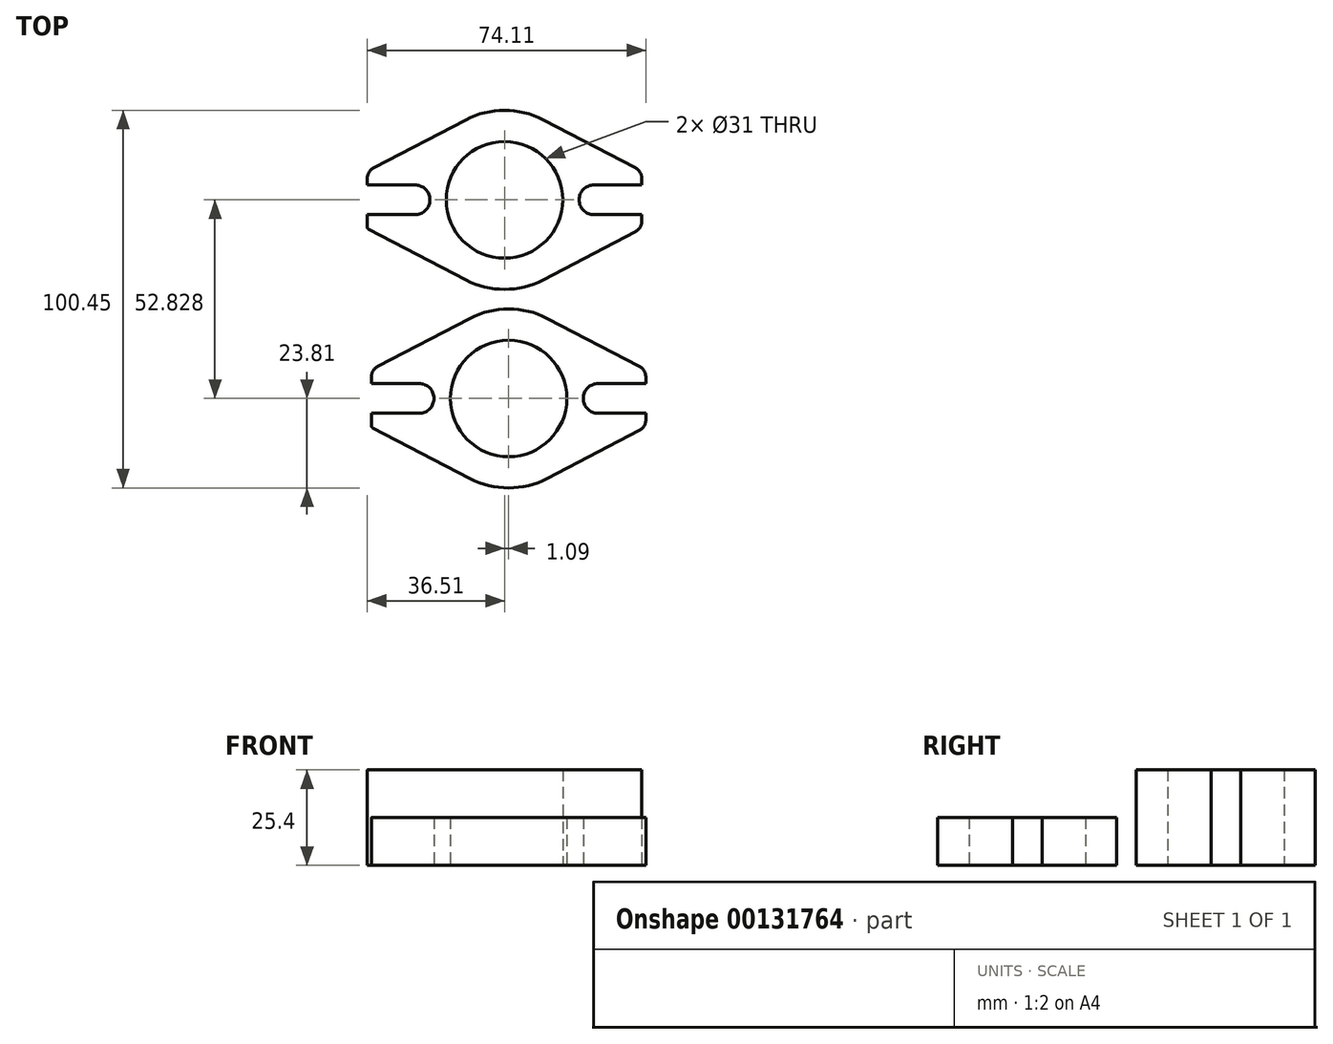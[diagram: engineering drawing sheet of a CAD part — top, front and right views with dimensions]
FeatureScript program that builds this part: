
annotation { "Feature Type Name" : "Feature", "Feature Type Description" : "" }
export const myFeature = defineFeature(function(context is Context, id is Id, definition is map)
    precondition{}
    {
        {
            var Q0;
            Q0=qCreatedBy(makeId("Top.planeOp"), FACE);
            var sketch = newSketch(context, id + "F0", { "sketchPlane" : qUnion([Q0])});
            skLineSegment(sketch, "E0.left", {"start": v(36.51, -5.7) * mm, "end": v(36.51, -3.96) * mm});
            skLineSegment(sketch, "E0.right", {"start": v(-36.51, -7.23) * mm, "end": v(-36.51, -3.96) * mm});
            skPoint(sketch, "E0.middle", {"position": v(0, 0) * mm});
            skArc(sketch, "E1", {"start": v(-23.81, -3.96) * mm, "mid": v(-19.85, 0) * mm, "end": v(-23.81, 3.96) * mm});
            skArc(sketch, "E2", {"start": v(23.81, 3.96) * mm, "mid": v(19.85, 0) * mm, "end": v(23.81, -3.96) * mm});
            skLineSegment(sketch, "E3", {"start": v(-36.51, 3.96) * mm, "end": v(-23.81, 3.96) * mm});
            skLineSegment(sketch, "E4", {"start": v(-36.51, -3.96) * mm, "end": v(-23.81, -3.96) * mm});
            skLineSegment(sketch, "E5", {"start": v(23.81, 3.96) * mm, "end": v(36.51, 3.96) * mm});
            skLineSegment(sketch, "E6", {"start": v(36.51, -3.96) * mm, "end": v(23.81, -3.96) * mm});
            skLineSegment(sketch, "E7.trimOffspring", {"start": v(36.51, 3.96) * mm, "end": v(36.51, 5.7) * mm});
            skLineSegment(sketch, "E8.trimOffspring", {"start": v(-36.51, 3.96) * mm, "end": v(-36.51, 5.7) * mm});
            skPoint(sketch, "E9", {"position": v(-36.51, 7.62) * mm});
            skPoint(sketch, "E10", {"position": v(-36.51, -7.62) * mm});
            skPoint(sketch, "E11", {"position": v(36.51, -7.62) * mm});
            skPoint(sketch, "E12", {"position": v(36.51, 7.62) * mm});
            skArc(sketch, "E13", {"start": v(10.27, 21.3) * mm, "mid": v(0, 23.81) * mm, "end": v(-10.27, 21.3) * mm});
            skArc(sketch, "E14", {"start": v(-10.27, -21.3) * mm, "mid": v(0, -23.81) * mm, "end": v(10.27, -21.3) * mm});
            skLineSegment(sketch, "E15", {"start": v(-36.17, -7.8) * mm, "end": v(-10.27, -21.3) * mm});
            skLineSegment(sketch, "E16", {"start": v(10.27, -21.3) * mm, "end": v(34.8, -8.5) * mm});
            skLineSegment(sketch, "E17", {"start": v(-34.8, 8.5) * mm, "end": v(-10.27, 21.3) * mm});
            skLineSegment(sketch, "E18", {"start": v(10.27, 21.3) * mm, "end": v(34.8, 8.5) * mm});
            skPoint(sketch, "E19.orphan", {"position": v(-36.51, 23.81) * mm});
            skPoint(sketch, "E20.orphan", {"position": v(36.51, 23.81) * mm});
            skPoint(sketch, "E21.orphan", {"position": v(36.51, -23.81) * mm});
            skPoint(sketch, "E22.orphan", {"position": v(-36.51, -23.81) * mm});
            skArc(sketch, "E23.filletArc", {"start": v(-34.8, 8.5) * mm, "mid": v(-36.05, 7.34) * mm, "end": v(-36.51, 5.7) * mm});
            skArc(sketch, "E24.filletArc", {"start": v(-36.51, -7.23) * mm, "mid": v(-36.42, -7.56) * mm, "end": v(-36.17, -7.8) * mm});
            skArc(sketch, "E25.filletArc", {"start": v(34.8, -8.5) * mm, "mid": v(36.05, -7.34) * mm, "end": v(36.51, -5.7) * mm});
            skArc(sketch, "E26.filletArc", {"start": v(36.51, 5.7) * mm, "mid": v(36.05, 7.34) * mm, "end": v(34.8, 8.5) * mm});
            skCircle(sketch, "E27", {"center": v(0, 0) * mm, "radius": 15.5 * mm});
            skSolve(sketch);
        }
        {
            var Q0;
            Q0 = qSketchRegion(id + "F0", true);
            extrude(context, id + "F1", {"entities" : qUnion([Q0]), "depth" : 12.7 * mm, "offsetDistance" : 25.4 * mm});
        }
        {
            var Q0;
            Q0=qCreatedBy(makeId("Top.planeOp"), FACE);
            var sketch = newSketch(context, id + "F2", { "sketchPlane" : qUnion([Q0])});
            skLineSegment(sketch, "E28.left", {"start": v(35.42, 47.13) * mm, "end": v(35.42, 48.87) * mm});
            skLineSegment(sketch, "E28.right", {"start": v(-37.6, 45.6) * mm, "end": v(-37.6, 48.87) * mm});
            skPoint(sketch, "E28.middle", {"position": v(-1.09, 52.83) * mm});
            skArc(sketch, "E29", {"start": v(-24.9, 48.87) * mm, "mid": v(-20.94, 52.83) * mm, "end": v(-24.9, 56.8) * mm});
            skArc(sketch, "E30", {"start": v(22.72, 56.8) * mm, "mid": v(18.76, 52.83) * mm, "end": v(22.72, 48.87) * mm});
            skLineSegment(sketch, "E31", {"start": v(-37.6, 56.8) * mm, "end": v(-24.9, 56.8) * mm});
            skLineSegment(sketch, "E32", {"start": v(-37.6, 48.87) * mm, "end": v(-24.9, 48.87) * mm});
            skLineSegment(sketch, "E33", {"start": v(22.72, 56.8) * mm, "end": v(35.42, 56.8) * mm});
            skLineSegment(sketch, "E34", {"start": v(35.42, 48.87) * mm, "end": v(22.72, 48.87) * mm});
            skLineSegment(sketch, "E35.trimOffspring", {"start": v(35.42, 56.8) * mm, "end": v(35.42, 58.52) * mm});
            skLineSegment(sketch, "E36.trimOffspring", {"start": v(-37.6, 56.8) * mm, "end": v(-37.6, 58.52) * mm});
            skPoint(sketch, "E37", {"position": v(-37.6, 60.45) * mm});
            skPoint(sketch, "E38", {"position": v(-37.6, 45.2) * mm});
            skPoint(sketch, "E39", {"position": v(35.42, 45.2) * mm});
            skPoint(sketch, "E40", {"position": v(35.42, 60.45) * mm});
            skArc(sketch, "E41", {"start": v(9.18, 74.12) * mm, "mid": v(-1.09, 76.64) * mm, "end": v(-11.36, 74.12) * mm});
            skArc(sketch, "E42", {"start": v(-11.36, 31.53) * mm, "mid": v(-1.09, 29.02) * mm, "end": v(9.18, 31.53) * mm});
            skLineSegment(sketch, "E43", {"start": v(-37.26, 45.03) * mm, "end": v(-11.36, 31.53) * mm});
            skLineSegment(sketch, "E44", {"start": v(9.18, 31.53) * mm, "end": v(33.72, 44.32) * mm});
            skLineSegment(sketch, "E45", {"start": v(-35.9, 61.34) * mm, "end": v(-11.36, 74.12) * mm});
            skLineSegment(sketch, "E46", {"start": v(9.18, 74.12) * mm, "end": v(33.72, 61.34) * mm});
            skPoint(sketch, "E47.orphan", {"position": v(-37.6, 76.64) * mm});
            skPoint(sketch, "E48.orphan", {"position": v(35.42, 76.64) * mm});
            skPoint(sketch, "E49.orphan", {"position": v(35.42, 29.02) * mm});
            skPoint(sketch, "E50.orphan", {"position": v(-37.6, 29.02) * mm});
            skArc(sketch, "E51.filletArc", {"start": v(-35.9, 61.34) * mm, "mid": v(-37.14, 60.17) * mm, "end": v(-37.6, 58.52) * mm});
            skArc(sketch, "E52.filletArc", {"start": v(-37.6, 45.6) * mm, "mid": v(-37.51, 45.26) * mm, "end": v(-37.26, 45.03) * mm});
            skArc(sketch, "E53.filletArc", {"start": v(33.72, 44.32) * mm, "mid": v(34.96, 45.49) * mm, "end": v(35.42, 47.13) * mm});
            skArc(sketch, "E54.filletArc", {"start": v(35.42, 58.52) * mm, "mid": v(34.96, 60.17) * mm, "end": v(33.72, 61.34) * mm});
            skCircle(sketch, "E55", {"center": v(-1.09, 52.83) * mm, "radius": 15.5 * mm});
            skSolve(sketch);
        }
        {
            var Q0;
            Q0 = qSketchRegion(id + "F2", true);
            extrude(context, id + "F3", {"entities" : qUnion([Q0]), "depth" : 25.4 * mm, "offsetDistance" : 25.4 * mm});
        }
    });
